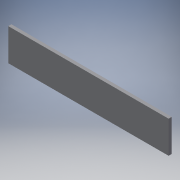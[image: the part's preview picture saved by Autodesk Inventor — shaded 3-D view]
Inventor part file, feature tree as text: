
AUTODESK INVENTOR PART (.ipt)
format: ipt  version: 2019 (Build 230136000, 136)  size: 97,280 bytes
history: native  units: mm
features: extrude x1, sketch x1
ambient origin geometry x8: Origin, YZ Plane, XZ Plane, XY Plane, X Axis, Y Axis, Z Axis, Center Point
bodies: Solid1 (feature_tree)
feature tree (2):
  extrude  "Extrusion1"  Depth=500.0mm
  sketch  "Sketch1"  dims[d0=5.5mm d1=500.0mm d2=100.0mm d3=10.0mm d4=0.0mm]
